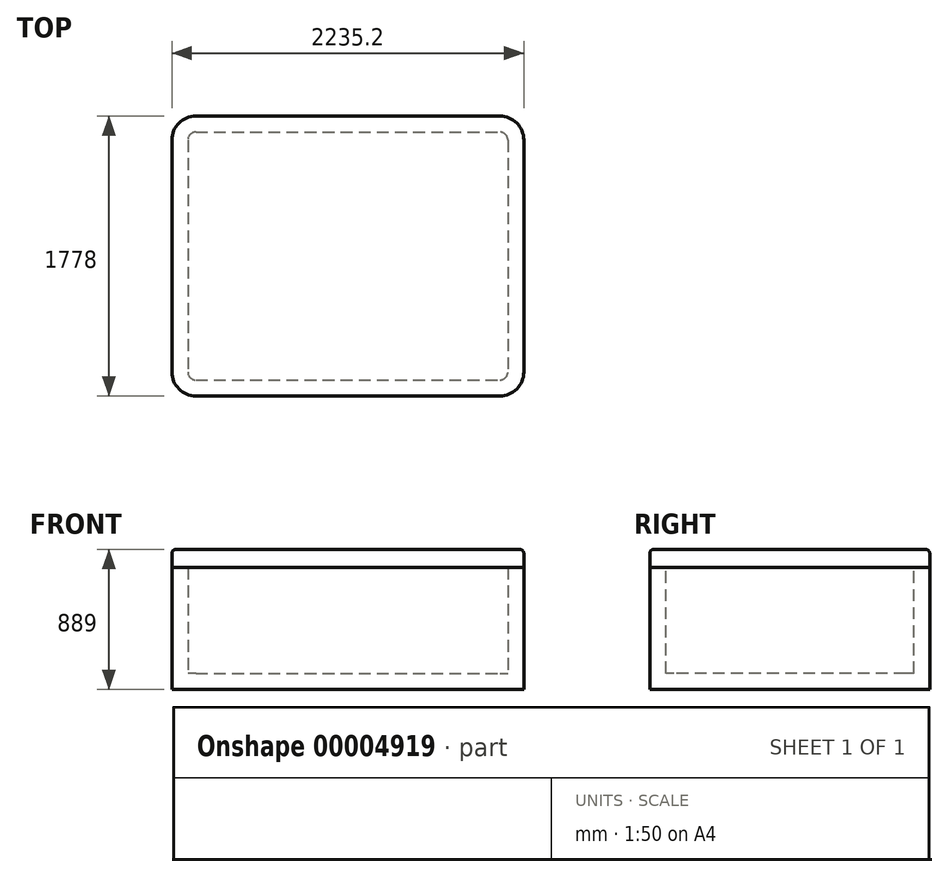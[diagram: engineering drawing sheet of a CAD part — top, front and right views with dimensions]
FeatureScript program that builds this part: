
annotation { "Feature Type Name" : "Feature", "Feature Type Description" : "" }
export const myFeature = defineFeature(function(context is Context, id is Id, definition is map)
    precondition{}
    {
        {
            var Q0;
            Q0=qCreatedBy(makeId("Top.planeOp"),FACE);
            var sketch = newSketch(context, id + "F0", { "sketchPlane" : qUnion([Q0])});
            skLineSegment(sketch, "E0.rect.bottom", {"start": v(-1117.6, 889) * mm, "end": v(1117.6, 889) * mm});
            skLineSegment(sketch, "E0.rect.top", {"start": v(-1117.6, -889) * mm, "end": v(1117.6, -889) * mm});
            skLineSegment(sketch, "E0.rect.left", {"start": v(-1117.6, 889) * mm, "end": v(-1117.6, -889) * mm});
            skLineSegment(sketch, "E0.rect.right", {"start": v(1117.6, 889) * mm, "end": v(1117.6, -889) * mm});
            skPoint(sketch, "E0.rect.middle", {"position": v(0, 0) * mm});
            skSolve(sketch);
        }
        {
            var Q0;
            Q0 = qSketchRegion(id + "F0", true);
            extrude(context, id + "F1", {"entities" : qUnion([Q0]), "depth" : 774.7 * mm});
        }
        {
            var Q0;
            Q0=makeQuery(id+"F1.opExtrude","SWEPT_EDGE",EDGE,{"disambiguationData":[OSD([sQuery(id+"F0.wireOp",EDGE,"E0.rect.top"),sQuery(id+"F0.wireOp",EDGE,"E0.rect.right")])]});
            var Q1;
            Q1=makeQuery(id+"F1.opExtrude","SWEPT_EDGE",EDGE,{"disambiguationData":[OSD([sQuery(id+"F0.wireOp",EDGE,"E0.rect.top"),sQuery(id+"F0.wireOp",EDGE,"E0.rect.left")])]});
            var Q2;
            Q2=makeQuery(id+"F1.opExtrude","SWEPT_EDGE",EDGE,{"disambiguationData":[OSD([sQuery(id+"F0.wireOp",EDGE,"E0.rect.bottom"),sQuery(id+"F0.wireOp",EDGE,"E0.rect.left")])]});
            var Q3;
            Q3=makeQuery(id+"F1.opExtrude","SWEPT_EDGE",EDGE,{"disambiguationData":[OSD([sQuery(id+"F0.wireOp",EDGE,"E0.rect.bottom"),sQuery(id+"F0.wireOp",EDGE,"E0.rect.right")])]});
            fillet(context, id + "F2", {"entities" : qUnion([Q0, Q1, Q2, Q3]), "radius" : 152.4 * mm, "tangentPropagation" : true, "allowEdgeOverflow" : false});
        }
        {
            var Q0;
            Q0=makeQuery(id+"F1.opExtrude","CAP_FACE",FACE,{"disambiguationData":[OSD([sQuery(id+"F0.wireOp",EDGE,"E0.rect.bottom"),sQuery(id+"F0.wireOp",EDGE,"E0.rect.top"),sQuery(id+"F0.wireOp",EDGE,"E0.rect.left"),sQuery(id+"F0.wireOp",EDGE,"E0.rect.right")])],"isStart":false});
            shell(context, id + "F3", {"entities" : qUnion([Q0]), "thickness" : 101.6 * mm});
        }
        {
            var Q0;
            Q0=makeQuery(id+"F1.opExtrude","CAP_FACE",FACE,{"disambiguationData":[OSD([sQuery(id+"F0.wireOp",EDGE,"E0.rect.bottom"),sQuery(id+"F0.wireOp",EDGE,"E0.rect.top"),sQuery(id+"F0.wireOp",EDGE,"E0.rect.left"),sQuery(id+"F0.wireOp",EDGE,"E0.rect.right")])],"isStart":false});
            var sketch = newSketch(context, id + "F4", { "sketchPlane" : qUnion([Q0])});
            skLineSegment(sketch, "E1.0", {"start": v(-965.2, 889) * mm, "end": v(965.2, 889) * mm});
            skArc(sketch, "E2.0", {"start": v(-965.2, 889) * mm, "mid": v(-1072.96, 844.36) * mm, "end": v(-1117.6, 736.6) * mm});
            skLineSegment(sketch, "E3.0", {"start": v(-1117.6, 736.6) * mm, "end": v(-1117.6, -736.6) * mm});
            skArc(sketch, "E4.0", {"start": v(-1117.6, -736.6) * mm, "mid": v(-1072.96, -844.36) * mm, "end": v(-965.2, -889) * mm});
            skLineSegment(sketch, "E5.0", {"start": v(-965.2, -889) * mm, "end": v(965.2, -889) * mm});
            skArc(sketch, "E6.0", {"start": v(965.2, -889) * mm, "mid": v(1072.96, -844.36) * mm, "end": v(1117.6, -736.6) * mm});
            skLineSegment(sketch, "E7.0", {"start": v(1117.6, 736.6) * mm, "end": v(1117.6, -736.6) * mm});
            skArc(sketch, "E8.0", {"start": v(1117.6, 736.6) * mm, "mid": v(1072.96, 844.36) * mm, "end": v(965.2, 889) * mm});
            skSolve(sketch);
        }
        {
            var Q0;
            Q0 = qSketchRegion(id + "F4", true);
            extrude(context, id + "F5", {"entities" : qUnion([Q0]), "depth" : 114.3 * mm});
        }
        {
            var Q0;
            Q0=makeQuery(id+"F5.opExtrude","CAP_EDGE",EDGE,{"disambiguationData":[OSD([sQuery(id+"F4.wireOp",EDGE,"E5.0")])],"isStart":false});
            fillet(context, id + "F6", {"entities" : qUnion([Q0]), "radius" : 25.4 * mm, "tangentPropagation" : true, "allowEdgeOverflow" : false});
        }
        {
            var Q0;
            Q0=makeQuery(id+"F1.opExtrude","CAP_FACE",FACE,{"disambiguationData":[OSD([sQuery(id+"F0.wireOp",EDGE,"E0.rect.bottom"),sQuery(id+"F0.wireOp",EDGE,"E0.rect.top"),sQuery(id+"F0.wireOp",EDGE,"E0.rect.left"),sQuery(id+"F0.wireOp",EDGE,"E0.rect.right")])],"isStart":true});
            var sketch = newSketch(context, id + "F7", { "sketchPlane" : qUnion([Q0])});
            skLineSegment(sketch, "E9.0", {"start": v(-965.2, -889) * mm, "end": v(1117.6, -889) * mm});
            skLineSegment(sketch, "E10.0", {"start": v(1117.6, -889) * mm, "end": v(1117.6, 736.6) * mm});
            skPoint(sketch, "E11.orphan", {"position": v(965.2, -889) * mm});
            skPoint(sketch, "E12.orphan", {"position": v(1117.6, -736.6) * mm});
            skSolve(sketch);
        }
    });
